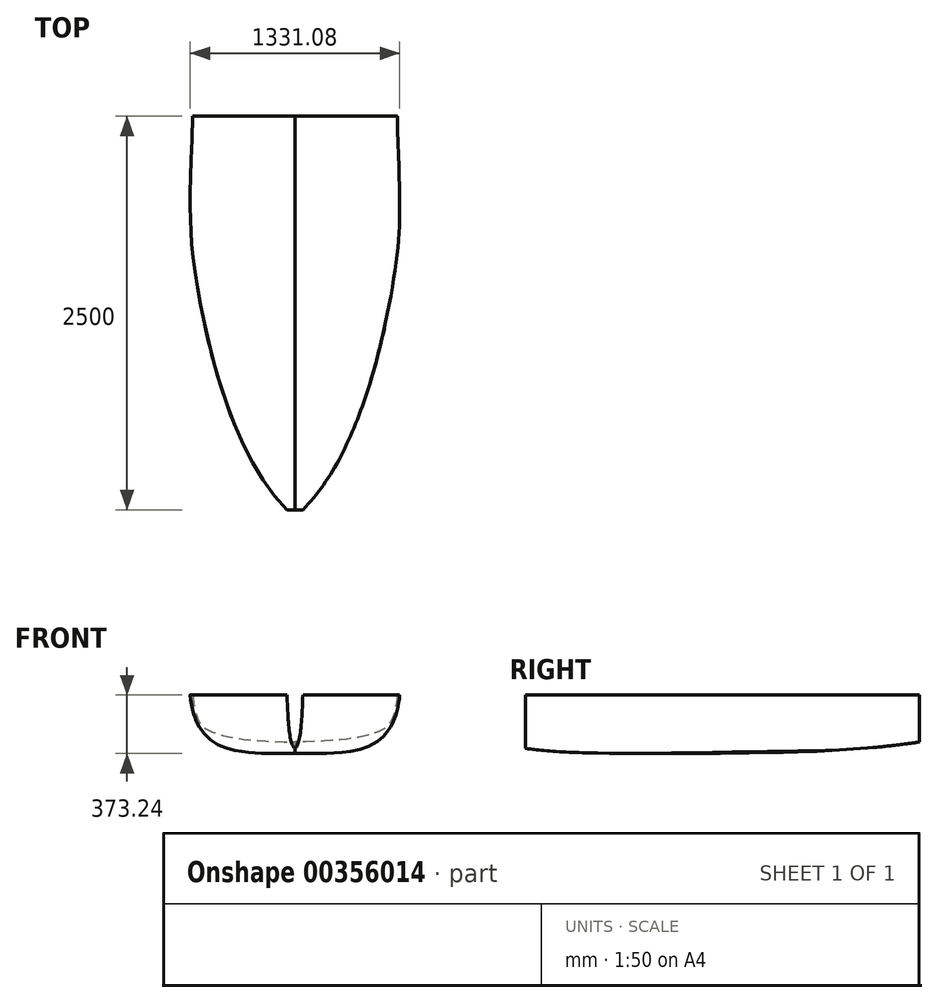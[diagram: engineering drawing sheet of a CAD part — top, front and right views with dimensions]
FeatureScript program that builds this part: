
annotation { "Feature Type Name" : "Feature", "Feature Type Description" : "" }
export const myFeature = defineFeature(function(context is Context, id is Id, definition is map)
    precondition{}
    {
        {
            var Q0;
            Q0=qCreatedBy(makeId("Front.planeOp"),FACE);
            cPlane(context, id + "F0", {"entities" : qUnion([Q0]), "cplaneType" : CPlaneType.OFFSET, "offset" : 1000 * mm, "width" : 150 * mm, "height" : 150 * mm});
        }
        {
            var Q0;
            Q0=qCreatedBy(makeId("Front.planeOp"),FACE);
            var sketch = newSketch(context, id + "F1", { "sketchPlane" : qUnion([Q0])});
            skFitSpline(sketch, "E0", {"points": [v(-650, 0) * mm, v(-541.1, -228.02) * mm, v(0, -300) * mm], "startDerivative": vector(109.64, -1210.35) * mm, "endDerivative": vector(1634.2, -29.3) * mm});
            skSolve(sketch);
        }
        {
            var Q0;
            Q0=qCreatedBy(id+"F0.planeOp",FACE);
            var sketch = newSketch(context, id + "F2", { "sketchPlane" : qUnion([Q0])});
            skFitSpline(sketch, "E1", {"points": [v(-632, 0) * mm, v(-528.84, -276.4) * mm, v(0, -360) * mm], "startDerivative": vector(12.73, -383.24) * mm, "endDerivative": vector(1296.77, 58.82) * mm});
            skSolve(sketch);
        }
        {
            var Q0;
            Q0=qCreatedBy(makeId("Top.planeOp"),FACE);
            var sketch = newSketch(context, id + "F3", { "sketchPlane" : qUnion([Q0])});
            skFitSpline(sketch, "E2", {"points": [v(-650, 0) * mm, v(-632, -1000) * mm, v(-50, -2500) * mm], "startDerivative": vector(-112.28, -3666.7) * mm, "endDerivative": vector(1911.2, -1897.43) * mm});
            skSolve(sketch);
        }
        {
            var Q0;
            Q0=qCreatedBy(makeId("Right.planeOp"),FACE);
            var sketch = newSketch(context, id + "F4", { "sketchPlane" : qUnion([Q0])});
            skFitSpline(sketch, "E3", {"points": [v(-2500, -340) * mm, v(-1000, -360) * mm, v(0, -300) * mm], "startDerivative": vector(1804.2, -281.69) * mm, "endDerivative": vector(2888.18, 402.34) * mm});
            skSolve(sketch);
        }
        {
            var Q0;
            Q0=qCreatedBy(makeId("Front.planeOp"),FACE);
            cPlane(context, id + "F5", {"entities" : qUnion([Q0]), "cplaneType" : CPlaneType.OFFSET, "offset" : 2500 * mm, "width" : 150 * mm, "height" : 150 * mm});
        }
        {
            var Q0;
            Q0=qCreatedBy(id+"F5.planeOp",FACE);
            var sketch = newSketch(context, id + "F6", { "sketchPlane" : qUnion([Q0])});
            skFitSpline(sketch, "E4", {"points": [v(-50, 0) * mm, v(0, -340) * mm], "startDerivative": vector(15.71, -443.95) * mm, "endDerivative": vector(116.25, -69.36) * mm});
            skSolve(sketch);
        }
        {
            var Q0;
            Q0=sQuery(id+"F1.wireOp",EDGE,"E0");
            var Q1;
            Q1=sQuery(id+"F2.wireOp",EDGE,"E1");
            var Q2;
            Q2=sQuery(id+"F6.wireOp",EDGE,"E4");
            var Q3;
            Q3=sQuery(id+"F3.wireOp",EDGE,"E2");
            var Q4;
            Q4=sQuery(id+"F4.wireOp",EDGE,"E3");
            loft(context, id + "F7", {"bodyType" : ToolBodyType.SURFACE, "addGuides" : true, "wireProfilesArray" : [{ "wireProfileEntities" : qUnion([Q0]) }, { "wireProfileEntities" : qUnion([Q1]) }, { "wireProfileEntities" : qUnion([Q2]) }], "guidesArray" : [{ "guideEntities" : qUnion([Q3]), "guideDerivativeType" : LoftGuideDerivativeType.DEFAULT, "guideDerivativeMagnitude" : 1 }, { "guideEntities" : qUnion([Q4]), "guideDerivativeType" : LoftGuideDerivativeType.DEFAULT, "guideDerivativeMagnitude" : 1 }]});
        }
        {
            var Q0;
            Q0=makeQuery(id+"F7.opLoft","SWEPT_BODY",BODY,{"disambiguationData":[OSD([sQuery(id+"F1.wireOp",EDGE,"E0"),sQuery(id+"F2.wireOp",EDGE,"E1"),sQuery(id+"F3.wireOp",EDGE,"E2"),sQuery(id+"F4.wireOp",EDGE,"E3"),sQuery(id+"F6.wireOp",EDGE,"E4")])]});
            var Q1;
            Q1=qCreatedBy(makeId("Right.planeOp"),FACE);
            mirror(context, id + "F8", {"entities" : qUnion([Q0]), "mirrorPlane" : qUnion([Q1])});
        }
    });
